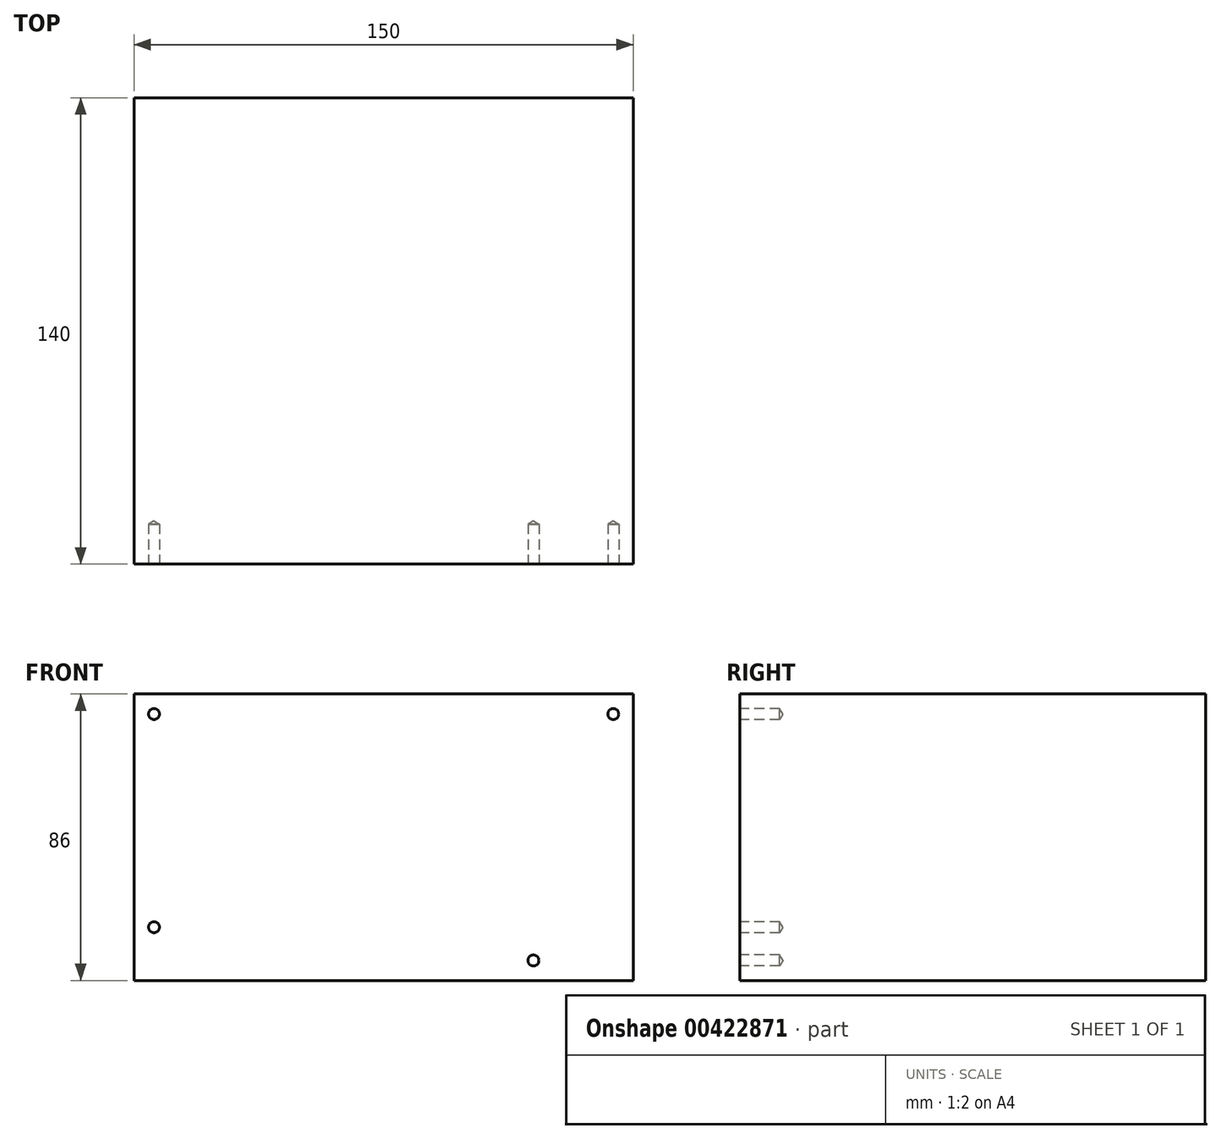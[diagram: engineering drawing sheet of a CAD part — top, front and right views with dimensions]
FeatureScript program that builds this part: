
annotation { "Feature Type Name" : "Feature", "Feature Type Description" : "" }
export const myFeature = defineFeature(function(context is Context, id is Id, definition is map)
    precondition{}
    {
        {
            var Q0;
            Q0=qCreatedBy(makeId("Front.planeOp"),FACE);
            var sketch = newSketch(context, id + "F0", { "sketchPlane" : qUnion([Q0])});
            skLineSegment(sketch, "E0.bottom", {"start": v(-75, -43) * mm, "end": v(75, -43) * mm});
            skLineSegment(sketch, "E0.top", {"start": v(-75, 43) * mm, "end": v(75, 43) * mm});
            skLineSegment(sketch, "E0.left", {"start": v(-75, -43) * mm, "end": v(-75, 43) * mm});
            skLineSegment(sketch, "E0.right", {"start": v(75, -43) * mm, "end": v(75, 43) * mm});
            skPoint(sketch, "E0.middle", {"position": v(0, 0) * mm});
            skPoint(sketch, "E1", {"position": v(69, 37) * mm});
            skPoint(sketch, "E2", {"position": v(-69, 37) * mm});
            skPoint(sketch, "E3", {"position": v(-69, -27) * mm});
            skPoint(sketch, "E4", {"position": v(45, -37) * mm});
            skSolve(sketch);
        }
        {
            var Q0;
            Q0=makeQuery(id+"F0.imprint","IMPRINT",FACE,{"disambiguationData":[TD([[makeQuery(id+"F0.imprint","IMPRINT",EDGE,{"derivedFrom":sQuery(id+"F0.wireOp",EDGE,"E0.bottom")}),1.0]])]});
            extrude(context, id + "F1", {"entities" : qUnion([Q0]), "oppositeDirection" : true, "depth" : 140 * mm});
        }
        {
            var Q0;
            Q0=sQuery(id+"F0.wireOp",VERTEX,"E2");
            var Q1;
            Q1=makeQuery(id+"F1.opExtrude","SWEPT_BODY",BODY,{"disambiguationData":[OSD([sQuery(id+"F0.wireOp",EDGE,"E0.bottom"),sQuery(id+"F0.wireOp",EDGE,"E0.top"),sQuery(id+"F0.wireOp",EDGE,"E0.left"),sQuery(id+"F0.wireOp",EDGE,"E0.right")])]});
            hole(context, id + "F2", {"style" : HoleStyle.SIMPLE, "endStyle" : HoleEndStyle.BLIND, "holeDiameter" : 3.3 * mm, "holeDepth" : 12 * mm, "isTappedThrough" : true, "tappedDepth" : 12 * mm, "tapClearance" : 3, "startFromSketch" : true, "locations" : qUnion([Q0]), "scope" : qUnion([Q1])});
        }
        {
            var Q0;
            Q0=sQuery(id+"F0.wireOp",VERTEX,"E3");
            var Q1;
            Q1=makeQuery(id+"F1.opExtrude","SWEPT_BODY",BODY,{"disambiguationData":[OSD([sQuery(id+"F0.wireOp",EDGE,"E0.bottom"),sQuery(id+"F0.wireOp",EDGE,"E0.top"),sQuery(id+"F0.wireOp",EDGE,"E0.left"),sQuery(id+"F0.wireOp",EDGE,"E0.right")])]});
            hole(context, id + "F3", {"style" : HoleStyle.SIMPLE, "endStyle" : HoleEndStyle.BLIND, "holeDiameter" : 3.3 * mm, "holeDepth" : 12 * mm, "isTappedThrough" : true, "tappedDepth" : 12 * mm, "tapClearance" : 3, "startFromSketch" : true, "locations" : qUnion([Q0]), "scope" : qUnion([Q1])});
        }
        {
            var Q0;
            Q0=sQuery(id+"F0.wireOp",VERTEX,"E1");
            var Q1;
            Q1=makeQuery(id+"F1.opExtrude","SWEPT_BODY",BODY,{"disambiguationData":[OSD([sQuery(id+"F0.wireOp",EDGE,"E0.bottom"),sQuery(id+"F0.wireOp",EDGE,"E0.top"),sQuery(id+"F0.wireOp",EDGE,"E0.left"),sQuery(id+"F0.wireOp",EDGE,"E0.right")])]});
            hole(context, id + "F4", {"style" : HoleStyle.SIMPLE, "endStyle" : HoleEndStyle.BLIND, "holeDiameter" : 3.3 * mm, "holeDepth" : 12 * mm, "isTappedThrough" : true, "tappedDepth" : 12 * mm, "tapClearance" : 3, "startFromSketch" : true, "locations" : qUnion([Q0]), "scope" : qUnion([Q1])});
        }
        {
            var Q0;
            Q0=sQuery(id+"F0.wireOp",VERTEX,"E4");
            var Q1;
            Q1=makeQuery(id+"F1.opExtrude","SWEPT_BODY",BODY,{"disambiguationData":[OSD([sQuery(id+"F0.wireOp",EDGE,"E0.bottom"),sQuery(id+"F0.wireOp",EDGE,"E0.top"),sQuery(id+"F0.wireOp",EDGE,"E0.left"),sQuery(id+"F0.wireOp",EDGE,"E0.right")])]});
            hole(context, id + "F5", {"style" : HoleStyle.SIMPLE, "endStyle" : HoleEndStyle.BLIND, "holeDiameter" : 3.3 * mm, "holeDepth" : 12 * mm, "isTappedThrough" : true, "tappedDepth" : 12 * mm, "tapClearance" : 3, "startFromSketch" : true, "locations" : qUnion([Q0]), "scope" : qUnion([Q1])});
        }
    });
